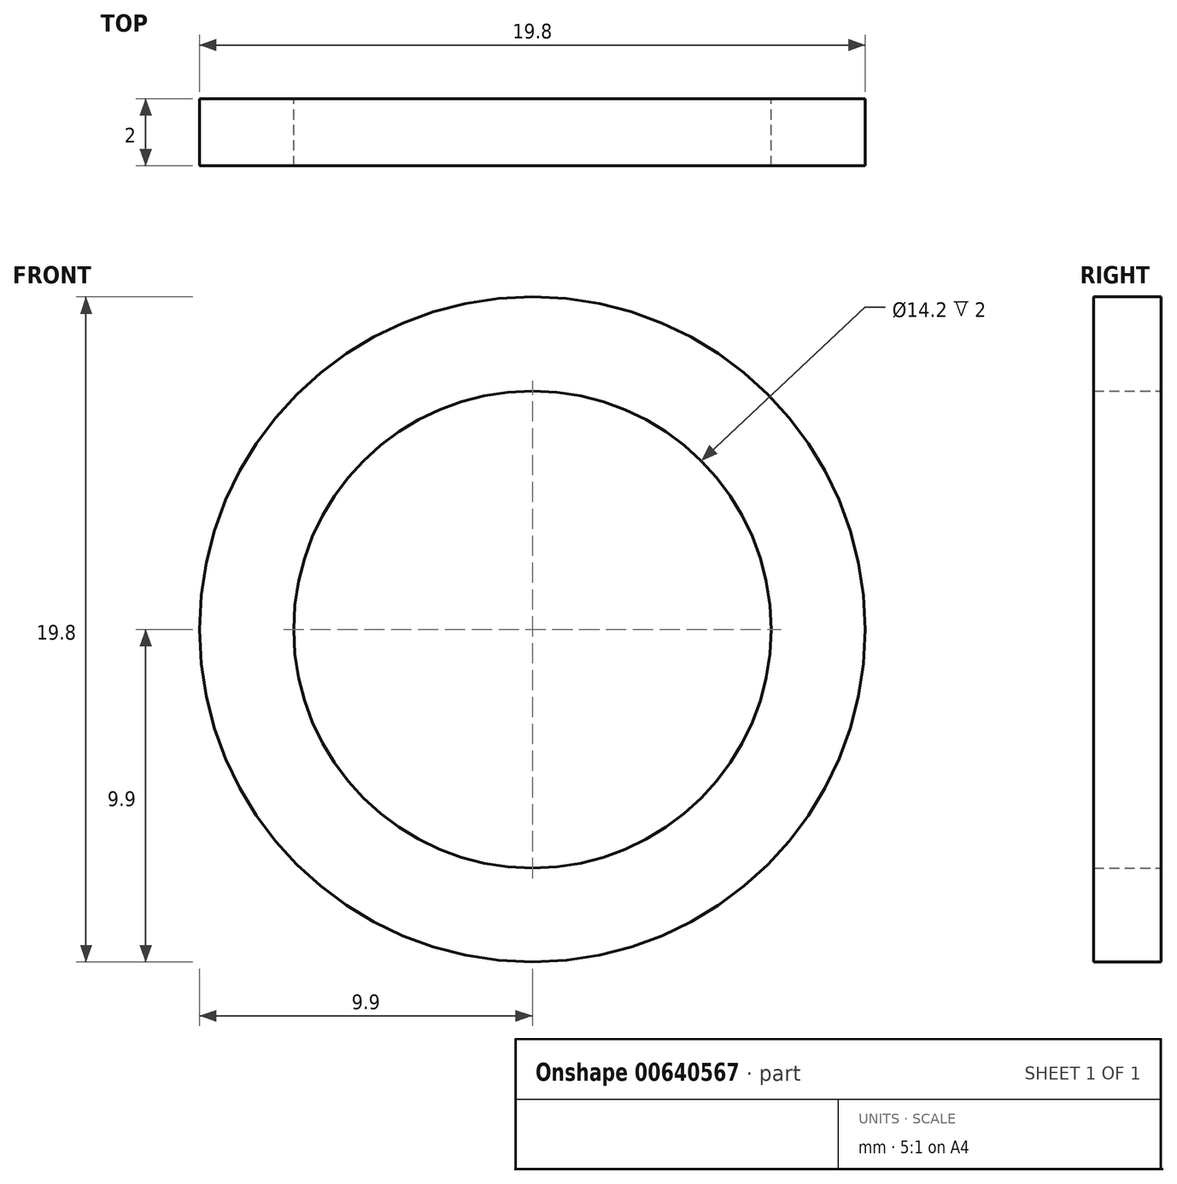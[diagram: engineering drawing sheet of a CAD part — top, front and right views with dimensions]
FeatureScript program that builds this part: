
annotation { "Feature Type Name" : "Feature", "Feature Type Description" : "" }
export const myFeature = defineFeature(function(context is Context, id is Id, definition is map)
    precondition{}
    {
        {
            var Q0;
            Q0=qCreatedBy(makeId("Front.planeOp"),FACE);
            var sketch = newSketch(context, id + "F0", { "sketchPlane" : qUnion([Q0])});
            skCircle(sketch, "E0", {"center": v(0, 0) * mm, "radius": 7.1 * mm});
            skCircle(sketch, "E1", {"center": v(0, 0) * mm, "radius": 9.9 * mm});
            skSolve(sketch);
        }
        {
            var Q0;
            Q0 = qSketchRegion(id + "F0", true);
            extrude(context, id + "F1", {"entities" : qUnion([Q0]), "depth" : 2 * mm, "offsetDistance" : 25 * mm});
        }
    });
